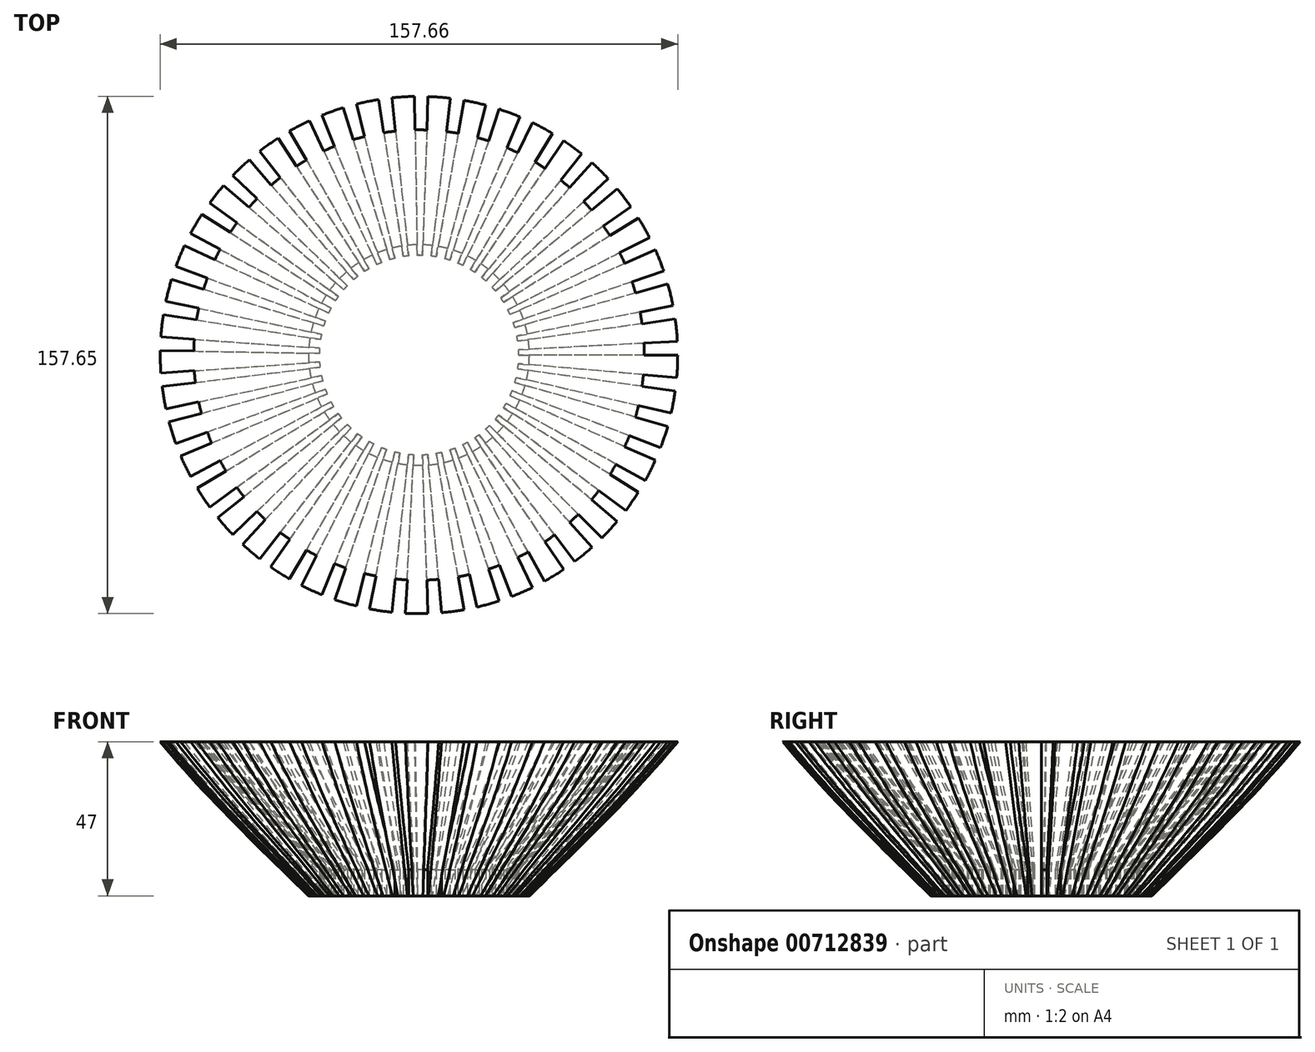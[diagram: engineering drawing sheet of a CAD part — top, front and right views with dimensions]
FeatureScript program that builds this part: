
annotation { "Feature Type Name" : "Feature", "Feature Type Description" : "" }
export const myFeature = defineFeature(function(context is Context, id is Id, definition is map)
    precondition{}
    {
        {
            var Q0;
            Q0=qCreatedBy(makeId("Front.planeOp"),FACE);
            var sketch = newSketch(context, id + "F0", { "sketchPlane" : qUnion([Q0])});
            skFitSpline(sketch, "E0", {"points": [v(15, 200.17) * mm, v(37.76, 163.97) * mm, v(95.69, 133.97) * mm, v(100.86, 82.24) * mm, v(33.62, 0) * mm], "startDerivative": vector(72.35, -199.22) * mm, "endDerivative": vector(-262.9, -254.38) * mm});
            skLineSegment(sketch, "E1", {"start": v(15, 200.17) * mm, "end": v(0, 200.17) * mm});
            skLineSegment(sketch, "E2", {"start": v(0, 200.17) * mm, "end": v(0, 0) * mm});
            skLineSegment(sketch, "E3", {"start": v(0, 0) * mm, "end": v(33.62, 0) * mm});
            skFitSpline(sketch, "E4.0", {"points": [v(7.48, 197.44) * mm, v(8.23, 195.37) * mm, v(9.77, 191.14) * mm, v(12.33, 184.68) * mm, v(15.37, 178.18) * mm, v(18.48, 172.85) * mm, v(21.43, 168.72) * mm, v(23.89, 165.7) * mm, v(26.63, 162.8) * mm, v(29.15, 160.51) * mm, v(31.32, 158.76) * mm, v(33.03, 157.5) * mm, v(34.8, 156.28) * mm, v(36.62, 155.13) * mm, v(38.48, 154.04) * mm, v(41, 152.65) * mm, v(45.52, 150.37) * mm, v(52.22, 147.45) * mm, v(60.36, 144.21) * mm, v(68.31, 141.05) * mm, v(75.77, 137.8) * mm, v(81.28, 134.9) * mm, v(85.1, 132.45) * mm, v(87.22, 130.86) * mm, v(88.73, 129.57) * mm, v(89.78, 128.58) * mm, v(90.73, 127.58) * mm, v(91.92, 126.2) * mm, v(93.25, 124.36) * mm, v(94.6, 122.02) * mm, v(95.73, 119.5) * mm, v(96.93, 115.95) * mm, v(97.85, 111.09) * mm, v(98.03, 104.67) * mm, v(97.23, 97.8) * mm, v(95.77, 91.8) * mm, v(94.12, 86.92) * mm, v(92.66, 83.24) * mm, v(90.96, 79.53) * mm, v(88.4, 74.54) * mm, v(84.66, 68.24) * mm, v(79.38, 60.6) * mm, v(71.4, 50.3) * mm, v(59.9, 37.32) * mm, v(44.44, 21.6) * mm, v(33.54, 11.05) * mm, v(28.06, 5.75) * mm]});
            skLineSegment(sketch, "E4.1", {"start": v(9.41, 192.17) * mm, "end": v(8, 192.17) * mm});
            skLineSegment(sketch, "E4.2", {"start": v(8, 192.17) * mm, "end": v(8, 8) * mm});
            skLineSegment(sketch, "E4.3", {"start": v(8, 8) * mm, "end": v(30.38, 8) * mm});
            skLineSegment(sketch, "E5", {"start": v(30.38, 8) * mm, "end": v(30.38, 0) * mm});
            skLineSegment(sketch, "E6", {"start": v(9.41, 192.17) * mm, "end": v(9.41, 200.17) * mm});
            skLineSegment(sketch, "E7", {"start": v(8, 8) * mm, "end": v(0, 8) * mm});
            skSolve(sketch);
        }
        {
            var Q0;
            Q0=qCreatedBy(makeId("Top.planeOp"),FACE);
            var sketch = newSketch(context, id + "F1", { "sketchPlane" : qUnion([Q0])});
            skPoint(sketch, "E8.0", {"position": v(15, 0) * mm});
            skCircle(sketch, "E9", {"center": v(0, 0) * mm, "radius": 15 * mm});
            skSolve(sketch);
        }
        {
            var Q0;
            Q0=makeQuery(id+"F0.imprint","IMPRINT",FACE,{"disambiguationData":[TD([[makeQuery(id+"F0.imprint","IMPRINT",EDGE,{"derivedFrom":sQuery(id+"F0.wireOp",EDGE,"E0")}),-1.0]])]});
            var Q1;
            Q1=sQuery(id+"F0.wireOp",EDGE,"E2");
            revolve(context, id + "F2", {"surfaceOperationType" : NewSurfaceOperationType.NEW, "entities" : qUnion([Q0]), "axis" : qUnion([Q1]), "revolveType" : RevolveType.ONE_DIRECTION, "angle" : 5 * degree});
        }
        {
            var Q0;
            Q0=makeQuery(id+"F0.imprint","IMPRINT",FACE,{"disambiguationData":[TD([[makeQuery(id+"F0.imprint","IMPRINT",EDGE,{"derivedFrom":sQuery(id+"F0.wireOp",EDGE,"E4.0")}),-1.0]])]});
            var Q1;
            Q1=makeQuery(id+"F0.imprint","IMPRINT",FACE,{"disambiguationData":[TD([[makeQuery(id+"F0.imprint","IMPRINT",EDGE,{"derivedFrom":sQuery(id+"F0.wireOp",EDGE,"E4.1")}),-1.0]])]});
            var Q2;
            Q2=makeQuery(id+"F0.imprint","IMPRINT",FACE,{"disambiguationData":[TD([[makeQuery(id+"F0.imprint","IMPRINT",EDGE,{"derivedFrom":sQuery(id+"F0.wireOp",EDGE,"E4.3")}),-1.0]])]});
            var Q3;
            Q3=sQuery(id+"F0.wireOp",EDGE,"E2");
            revolve(context, id + "F3", {"surfaceOperationType" : NewSurfaceOperationType.NEW, "entities" : qUnion([Q0, Q1, Q2]), "axis" : qUnion([Q3]), "revolveType" : RevolveType.FULL});
        }
        {
            var Q0;
            Q0=makeQuery(id+"F2.opRevolve","SWEPT_BODY",BODY,{"disambiguationData":[OSD([sQuery(id+"F0.wireOp",EDGE,"E0"),sQuery(id+"F0.wireOp",EDGE,"E1"),sQuery(id+"F0.wireOp",EDGE,"E2"),sQuery(id+"F0.wireOp",EDGE,"E3")])]});
            var Q1;
            Q1=sQuery(id+"F0.wireOp",EDGE,"E2");
            circularPattern(context, id + "F4", {"operationType" : NewBodyOperationType.ADD, "entities" : qUnion([Q0]), "axis" : qUnion([Q1]), "angle" : 360 * degree, "instanceCount" : 45, "equalSpace" : true});
        }
        {
            var Q0;
            Q0=qCreatedBy(makeId("Top.planeOp"),FACE);
            cPlane(context, id + "F5", {"entities" : qUnion([Q0]), "cplaneType" : CPlaneType.OFFSET, "offset" : 47 * mm, "width" : 150 * mm, "height" : 150 * mm});
        }
        {
            var Q0;
            Q0=qCreatedBy(id+"F5.planeOp",FACE);
            var sketch = newSketch(context, id + "F6", { "sketchPlane" : qUnion([Q0])});
            skCircle(sketch, "E10", {"center": v(0, 0) * mm, "radius": 190.16 * mm});
            skSolve(sketch);
        }
        {
            var Q0;
            Q0=makeQuery(id+"F6.imprint","IMPRINT",FACE,{"disambiguationData":[TD([[makeQuery(id+"F6.imprint","IMPRINT",EDGE,{"derivedFrom":sQuery(id+"F6.wireOp",EDGE,"E10")}),1.0]])]});
            var Q1;
            {var subQ0=sQuery(id+"F0.wireOp",EDGE,"E1");var subQ1=makeQuery(id+"F2.opRevolve","SWEPT_FACE",FACE,{"disambiguationData":[OSD([subQ0])]});Q1=makeQuery(id+"F4.boolean.opBoolean","MERGE",FACE,{"derivedFrom":[subQ1,makeQuery(id+"F3.opRevolve","SWEPT_FACE",FACE,{"disambiguationData":[OSD([subQ0])]}),makeQuery(id+"F4.opPattern","COPY",FACE,{"derivedFrom":subQ1,"instanceName":"1"}),makeQuery(id+"F4.opPattern","COPY",FACE,{"derivedFrom":subQ1,"instanceName":"2"}),makeQuery(id+"F4.opPattern","COPY",FACE,{"derivedFrom":subQ1,"instanceName":"3"}),makeQuery(id+"F4.opPattern","COPY",FACE,{"derivedFrom":subQ1,"instanceName":"4"}),makeQuery(id+"F4.opPattern","COPY",FACE,{"derivedFrom":subQ1,"instanceName":"5"}),makeQuery(id+"F4.opPattern","COPY",FACE,{"derivedFrom":subQ1,"instanceName":"6"}),makeQuery(id+"F4.opPattern","COPY",FACE,{"derivedFrom":subQ1,"instanceName":"7"}),makeQuery(id+"F4.opPattern","COPY",FACE,{"derivedFrom":subQ1,"instanceName":"8"}),makeQuery(id+"F4.opPattern","COPY",FACE,{"derivedFrom":subQ1,"instanceName":"9"}),makeQuery(id+"F4.opPattern","COPY",FACE,{"derivedFrom":subQ1,"instanceName":"10"}),makeQuery(id+"F4.opPattern","COPY",FACE,{"derivedFrom":subQ1,"instanceName":"11"}),makeQuery(id+"F4.opPattern","COPY",FACE,{"derivedFrom":subQ1,"instanceName":"12"}),makeQuery(id+"F4.opPattern","COPY",FACE,{"derivedFrom":subQ1,"instanceName":"13"}),makeQuery(id+"F4.opPattern","COPY",FACE,{"derivedFrom":subQ1,"instanceName":"14"}),makeQuery(id+"F4.opPattern","COPY",FACE,{"derivedFrom":subQ1,"instanceName":"15"}),makeQuery(id+"F4.opPattern","COPY",FACE,{"derivedFrom":subQ1,"instanceName":"16"}),makeQuery(id+"F4.opPattern","COPY",FACE,{"derivedFrom":subQ1,"instanceName":"17"}),makeQuery(id+"F4.opPattern","COPY",FACE,{"derivedFrom":subQ1,"instanceName":"18"}),makeQuery(id+"F4.opPattern","COPY",FACE,{"derivedFrom":subQ1,"instanceName":"19"}),makeQuery(id+"F4.opPattern","COPY",FACE,{"derivedFrom":subQ1,"instanceName":"20"}),makeQuery(id+"F4.opPattern","COPY",FACE,{"derivedFrom":subQ1,"instanceName":"21"}),makeQuery(id+"F4.opPattern","COPY",FACE,{"derivedFrom":subQ1,"instanceName":"22"}),makeQuery(id+"F4.opPattern","COPY",FACE,{"derivedFrom":subQ1,"instanceName":"23"}),makeQuery(id+"F4.opPattern","COPY",FACE,{"derivedFrom":subQ1,"instanceName":"24"}),makeQuery(id+"F4.opPattern","COPY",FACE,{"derivedFrom":subQ1,"instanceName":"25"}),makeQuery(id+"F4.opPattern","COPY",FACE,{"derivedFrom":subQ1,"instanceName":"26"}),makeQuery(id+"F4.opPattern","COPY",FACE,{"derivedFrom":subQ1,"instanceName":"27"}),makeQuery(id+"F4.opPattern","COPY",FACE,{"derivedFrom":subQ1,"instanceName":"28"}),makeQuery(id+"F4.opPattern","COPY",FACE,{"derivedFrom":subQ1,"instanceName":"29"}),makeQuery(id+"F4.opPattern","COPY",FACE,{"derivedFrom":subQ1,"instanceName":"30"}),makeQuery(id+"F4.opPattern","COPY",FACE,{"derivedFrom":subQ1,"instanceName":"31"}),makeQuery(id+"F4.opPattern","COPY",FACE,{"derivedFrom":subQ1,"instanceName":"32"}),makeQuery(id+"F4.opPattern","COPY",FACE,{"derivedFrom":subQ1,"instanceName":"33"}),makeQuery(id+"F4.opPattern","COPY",FACE,{"derivedFrom":subQ1,"instanceName":"34"}),makeQuery(id+"F4.opPattern","COPY",FACE,{"derivedFrom":subQ1,"instanceName":"35"}),makeQuery(id+"F4.opPattern","COPY",FACE,{"derivedFrom":subQ1,"instanceName":"36"}),makeQuery(id+"F4.opPattern","COPY",FACE,{"derivedFrom":subQ1,"instanceName":"37"}),makeQuery(id+"F4.opPattern","COPY",FACE,{"derivedFrom":subQ1,"instanceName":"38"}),makeQuery(id+"F4.opPattern","COPY",FACE,{"derivedFrom":subQ1,"instanceName":"39"}),makeQuery(id+"F4.opPattern","COPY",FACE,{"derivedFrom":subQ1,"instanceName":"40"}),makeQuery(id+"F4.opPattern","COPY",FACE,{"derivedFrom":subQ1,"instanceName":"41"}),makeQuery(id+"F4.opPattern","COPY",FACE,{"derivedFrom":subQ1,"instanceName":"42"}),makeQuery(id+"F4.opPattern","COPY",FACE,{"derivedFrom":subQ1,"instanceName":"43"}),makeQuery(id+"F4.opPattern","COPY",FACE,{"derivedFrom":subQ1,"instanceName":"44"})]});}
            extrude(context, id + "F7", {"entities" : qUnion([Q0]), "operationType" : NewBodyOperationType.REMOVE, "endBound" : BoundingType.UP_TO_SURFACE, "depth" : 25 * mm, "endBoundEntityFace" : qUnion([Q1]), "offsetDistance" : 25 * mm});
        }
    });
